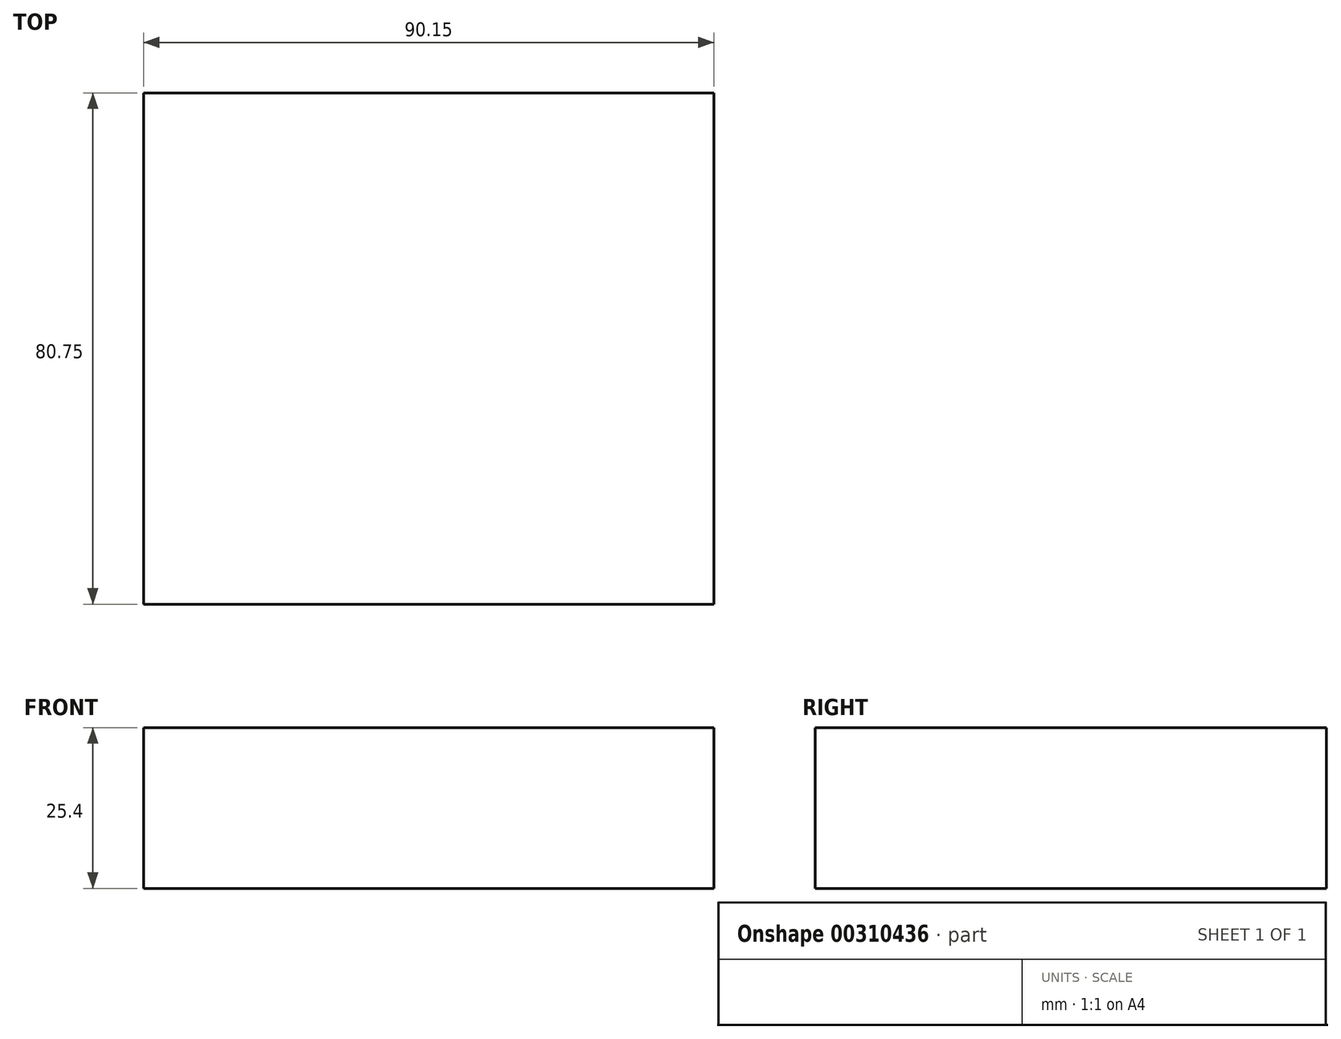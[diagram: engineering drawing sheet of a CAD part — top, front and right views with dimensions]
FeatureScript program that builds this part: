
annotation { "Feature Type Name" : "Feature", "Feature Type Description" : "" }
export const myFeature = defineFeature(function(context is Context, id is Id, definition is map)
    precondition{}
    {
        {
            var Q0;
            Q0=qCreatedBy(makeId("Top.planeOp"),FACE);
            var sketch = newSketch(context, id + "F0", { "sketchPlane" : qUnion([Q0])});
            skLineSegment(sketch, "E0.bottom", {"start": v(-42.59, 29.13) * mm, "end": v(47.56, 29.13) * mm});
            skLineSegment(sketch, "E0.top", {"start": v(-42.59, -51.62) * mm, "end": v(47.56, -51.62) * mm});
            skLineSegment(sketch, "E0.left", {"start": v(-42.59, 29.13) * mm, "end": v(-42.59, -51.62) * mm});
            skLineSegment(sketch, "E0.right", {"start": v(47.56, 29.13) * mm, "end": v(47.56, -51.62) * mm});
            skSolve(sketch);
        }
        {
            var Q0;
            Q0=makeQuery(id+"F0.imprint","IMPRINT",FACE,{"disambiguationData":[TD([[makeQuery(id+"F0.imprint","IMPRINT",EDGE,{"derivedFrom":sQuery(id+"F0.wireOp",EDGE,"E0.bottom")}),-1.0]])]});
            extrude(context, id + "F1", {"entities" : qUnion([Q0]), "depth" : 25.4 * mm});
        }
    });
